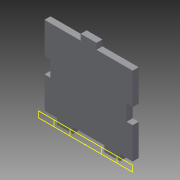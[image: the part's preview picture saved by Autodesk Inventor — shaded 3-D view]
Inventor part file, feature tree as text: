
AUTODESK INVENTOR PART (.ipt)
format: ipt  version: 2015 SP1 (Build 190203100, 203)  size: 130,560 bytes
history: native  units: in
note: dims shown in document units (in); Inventor stores cm internally (conversion verified against a paired STEP export)
features: reference x7, sketch x4, extrude x2, plane x1
ambient origin geometry x8: Origin, YZ Plane, XZ Plane, XY Plane, X Axis, Y Axis, Z Axis, Center Point
bodies: Solid1 (feature_tree)
feature tree (14):
  sketch  "Sketch1"  dims[d0=2.5in d2=0.5in]
  plane  "Work Plane1"
  extrude  "Extrusion1"  Depth=0.5in
  extrude  "Extrusion2"  Depth=0.19in
  sketch  "Sketch4"  dims[d8=0.5in d9=0.19in d10=1.15in d11=0.19in d12=0.0in d13=0.5in d14=0.25in d15=1.15in]
  reference  "Reference1"
  reference  "Reference2"
  reference  "Reference3"
  sketch  "Sketch2"  dims[d3=1.0in d5=0.19in]
  reference  "Reference4"
  reference  "Reference5"
  reference  "Reference6"
  reference  "Reference7"
  sketch  "Sketch3"  dims[d6=0.19in d7=0.0in]
